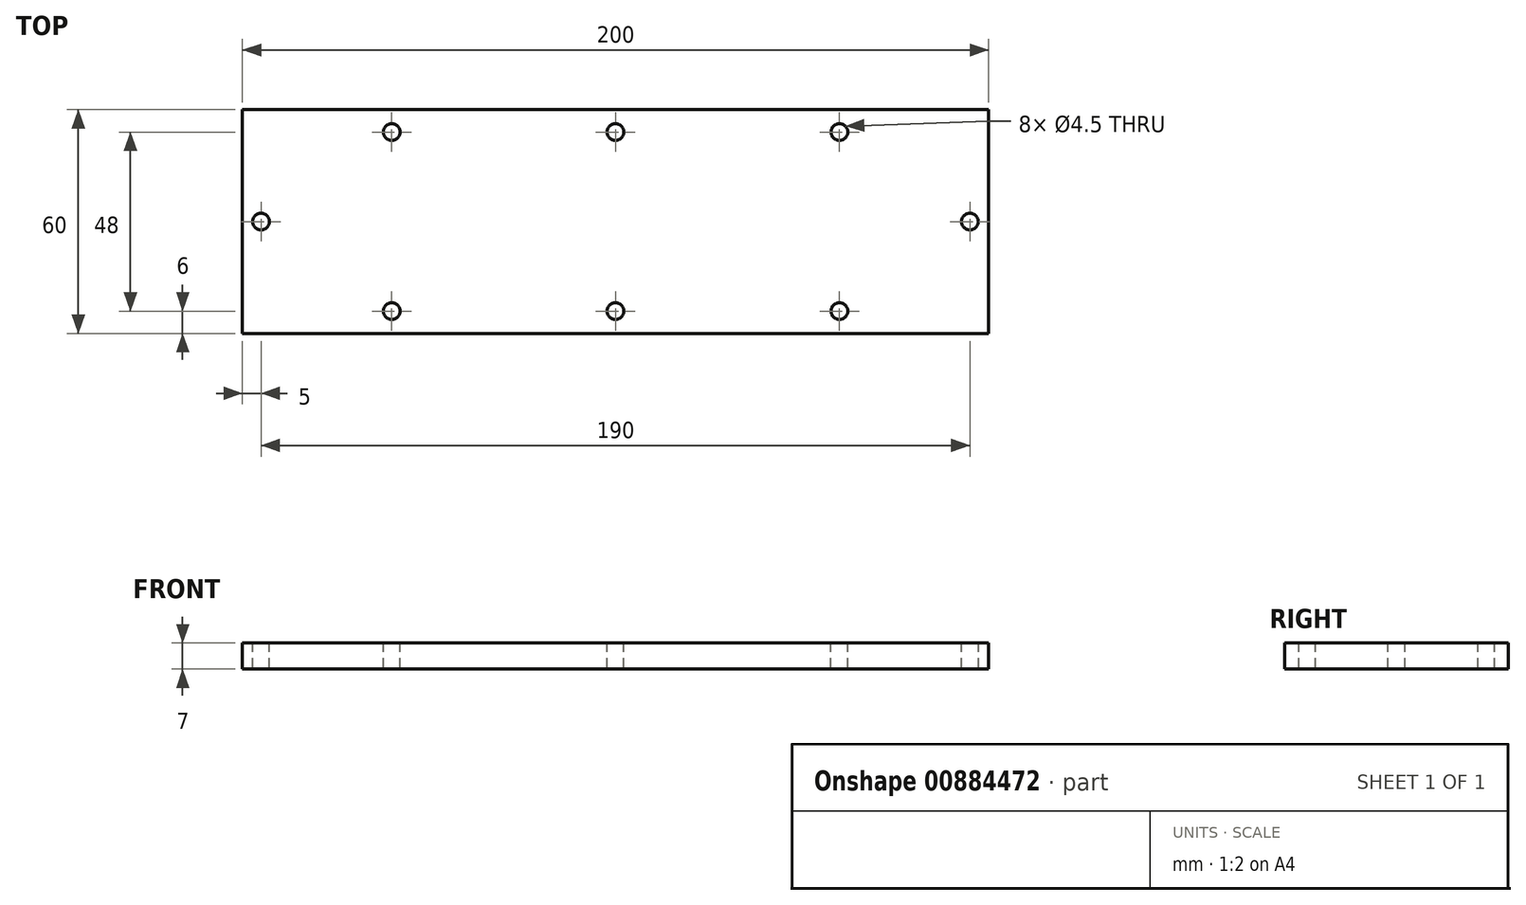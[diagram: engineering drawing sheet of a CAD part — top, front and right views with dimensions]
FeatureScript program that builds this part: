
annotation { "Feature Type Name" : "Feature", "Feature Type Description" : "" }
export const myFeature = defineFeature(function(context is Context, id is Id, definition is map)
    precondition{}
    {
        {
            var Q0;
            Q0=qCreatedBy(makeId("Top.planeOp"),FACE);
            var sketch = newSketch(context, id + "F0", { "sketchPlane" : qUnion([Q0])});
            skLineSegment(sketch, "E0.bottom", {"start": v(100, -30) * mm, "end": v(-100, -30) * mm});
            skLineSegment(sketch, "E0.top", {"start": v(100, 30) * mm, "end": v(-100, 30) * mm});
            skLineSegment(sketch, "E0.left", {"start": v(100, -30) * mm, "end": v(100, 30) * mm});
            skLineSegment(sketch, "E0.right", {"start": v(-100, -30) * mm, "end": v(-100, 30) * mm});
            skPoint(sketch, "E0.middle", {"position": v(0, 0) * mm});
            skLineSegment(sketch, "E1", {"start": v(-100, 0) * mm, "end": v(100, 0) * mm, "construction": true});
            skPoint(sketch, "E2", {"position": v(-95, 0) * mm});
            skPoint(sketch, "E3.MirrorP", {"position": v(95, 0) * mm});
            skLineSegment(sketch, "E4", {"start": v(0, 30) * mm, "end": v(0, -30) * mm, "construction": true});
            skLineSegment(sketch, "E5.bottom", {"start": v(60, -24) * mm, "end": v(-60, -24) * mm, "construction": true});
            skLineSegment(sketch, "E5.top", {"start": v(60, 24) * mm, "end": v(-60, 24) * mm, "construction": true});
            skLineSegment(sketch, "E5.left", {"start": v(60, -24) * mm, "end": v(60, 24) * mm, "construction": true});
            skLineSegment(sketch, "E5.right", {"start": v(-60, -24) * mm, "end": v(-60, 24) * mm, "construction": true});
            skPoint(sketch, "E6", {"position": v(0, 24) * mm});
            skPoint(sketch, "E7", {"position": v(0, -24) * mm});
            skSolve(sketch);
        }
        {
            var Q0;
            Q0=makeQuery(id+"F0.imprint","IMPRINT",FACE,{"disambiguationData":[TD([[makeQuery(id+"F0.imprint","IMPRINT",EDGE,{"derivedFrom":sQuery(id+"F0.wireOp",EDGE,"E0.bottom")}),-1.0]])]});
            extrude(context, id + "F1", {"entities" : qUnion([Q0]), "oppositeDirection" : true, "depth" : 7 * mm, "offsetDistance" : 25 * mm});
        }
        {
            var Q0;
            Q0=sQuery(id+"F0.wireOp",VERTEX,"E5.top.end");
            var Q1;
            Q1=sQuery(id+"F0.wireOp",VERTEX,"E5.top.start");
            var Q2;
            Q2=sQuery(id+"F0.wireOp",VERTEX,"E5.bottom.start");
            var Q3;
            Q3=sQuery(id+"F0.wireOp",VERTEX,"E5.bottom.end");
            var Q4;
            Q4=sQuery(id+"F0.wireOp",VERTEX,"E2");
            var Q5;
            Q5=sQuery(id+"F0.wireOp",VERTEX,"E3.MirrorP");
            var Q6;
            Q6=sQuery(id+"F0.wireOp",VERTEX,"E6");
            var Q7;
            Q7=sQuery(id+"F0.wireOp",VERTEX,"E7");
            var Q8;
            Q8=makeQuery(id+"F1.opExtrude","SWEPT_BODY",BODY,{"disambiguationData":[OSD([sQuery(id+"F0.wireOp",EDGE,"E0.bottom"),sQuery(id+"F0.wireOp",EDGE,"E0.top"),sQuery(id+"F0.wireOp",EDGE,"E0.left"),sQuery(id+"F0.wireOp",EDGE,"E0.right")])]});
            hole(context, id + "F2", {"style" : HoleStyle.SIMPLE, "endStyle" : HoleEndStyle.THROUGH, "standardTappedOrClearance" : lookupTablePath({ "fit" : "Normal", "standard" : "ISO", "size" : "M4", "type" : "Clearance" }), "standardBlindInLast" : lookupTablePath({ "fit" : "Normal", "standard" : "ISO", "size" : "M4", "type" : "Clearance" }), "holeDiameter" : 4.5 * mm, "majorDiameter" : 5 * mm, "isTappedThrough" : true, "tappedDepth" : 3.95 * mm, "tapClearance" : 3, "locations" : qUnion([Q0, Q1, Q2, Q3, Q4, Q5, Q6, Q7]), "scope" : qUnion([Q8])});
        }
    });
